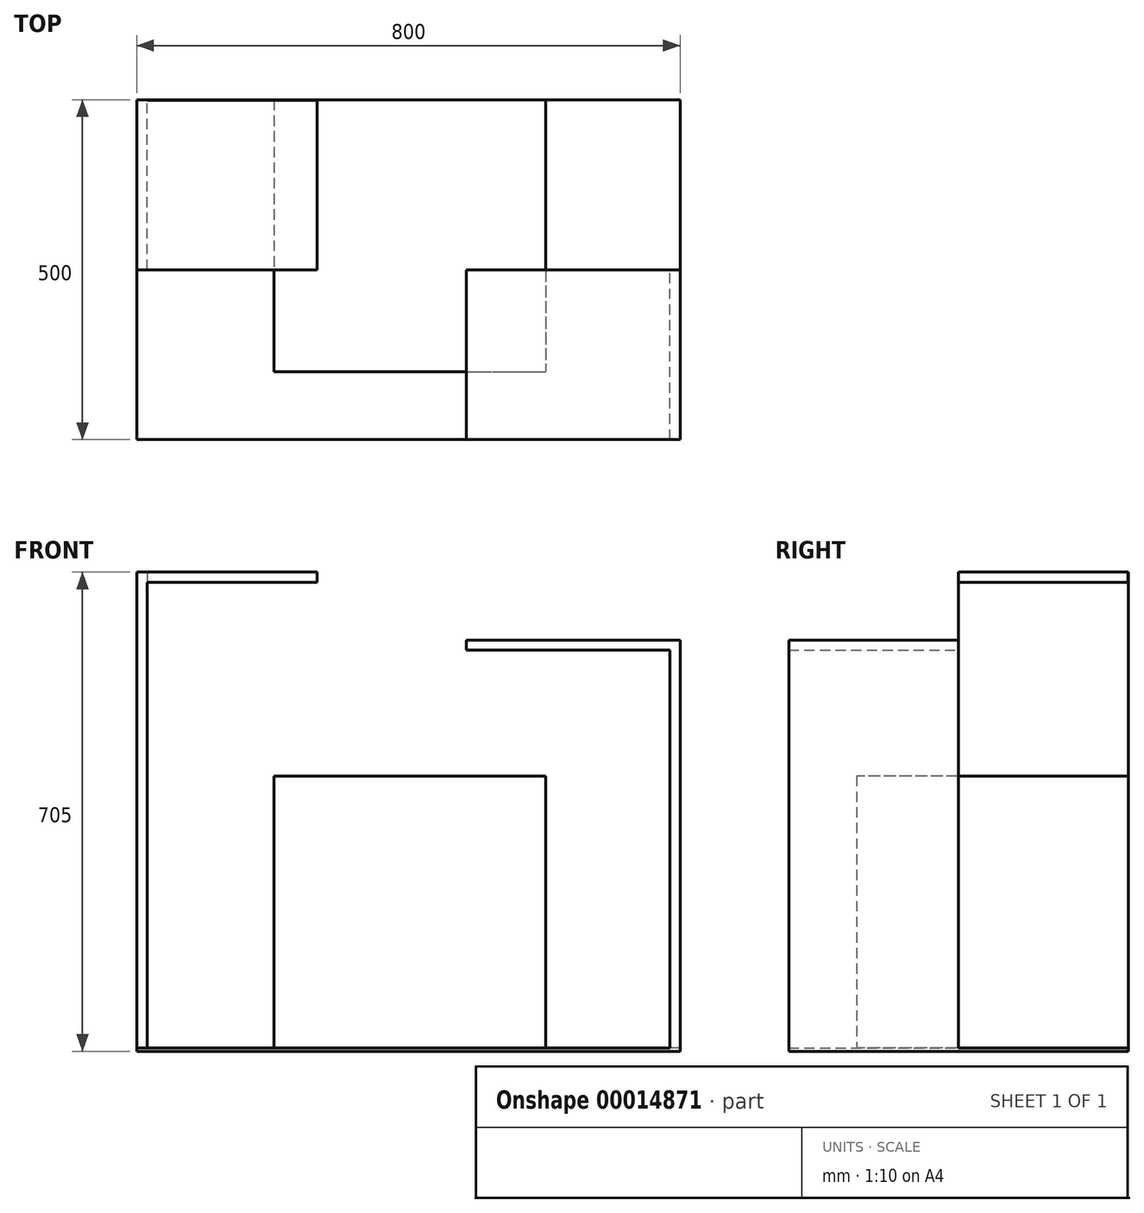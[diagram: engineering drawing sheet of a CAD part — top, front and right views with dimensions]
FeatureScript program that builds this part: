
annotation { "Feature Type Name" : "Feature", "Feature Type Description" : "" }
export const myFeature = defineFeature(function(context is Context, id is Id, definition is map)
    precondition{}
    {
        {
            var Q0;
            Q0=qCreatedBy(makeId("Top.planeOp"),FACE);
            var sketch = newSketch(context, id + "F0", { "sketchPlane" : qUnion([Q0])});
            skLineSegment(sketch, "E0.rect.bottom", {"start": v(-400, 250) * mm, "end": v(400, 250) * mm});
            skLineSegment(sketch, "E0.rect.top", {"start": v(-400, -250) * mm, "end": v(400, -250) * mm});
            skLineSegment(sketch, "E0.rect.left", {"start": v(-400, 250) * mm, "end": v(-400, -250) * mm});
            skLineSegment(sketch, "E0.rect.right", {"start": v(400, 250) * mm, "end": v(400, -250) * mm});
            skPoint(sketch, "E0.rect.middle", {"position": v(0, 0) * mm});
            skSolve(sketch);
        }
        {
            var Q0;
            Q0 = qSketchRegion(id + "F0", true);
            extrude(context, id + "F1", {"entities" : qUnion([Q0]), "depth" : 5 * mm});
        }
        {
            var Q0;
            Q0=makeQuery(id+"F1.opExtrude","CAP_FACE",FACE,{"disambiguationData":[OSD([sQuery(id+"F0.wireOp",EDGE,"E0.rect.bottom"),sQuery(id+"F0.wireOp",EDGE,"E0.rect.top"),sQuery(id+"F0.wireOp",EDGE,"E0.rect.left"),sQuery(id+"F0.wireOp",EDGE,"E0.rect.right")])],"isStart":false});
            cPlane(context, id + "F2", {"entities" : qUnion([Q0]), "cplaneType" : CPlaneType.OFFSET, "offset" : 0 * mm, "width" : 150 * mm, "height" : 150 * mm});
        }
        {
            var Q0;
            Q0=qCreatedBy(id+"F2.planeOp",FACE);
            var sketch = newSketch(context, id + "F3", { "sketchPlane" : qUnion([Q0])});
            skLineSegment(sketch, "E1.bottom", {"start": v(-198.2, 250) * mm, "end": v(201.8, 250) * mm});
            skLineSegment(sketch, "E1.top", {"start": v(-198.2, -150) * mm, "end": v(201.8, -150) * mm});
            skLineSegment(sketch, "E1.left", {"start": v(-198.2, 250) * mm, "end": v(-198.2, -150) * mm});
            skLineSegment(sketch, "E1.right", {"start": v(201.8, 250) * mm, "end": v(201.8, -150) * mm});
            skSolve(sketch);
        }
        {
            var Q0;
            Q0=makeQuery(id+"F3.imprint","IMPRINT",FACE,{"disambiguationData":[TD([[makeQuery(id+"F3.imprint","IMPRINT",EDGE,{"derivedFrom":sQuery(id+"F3.wireOp",EDGE,"E1.bottom")}),-1.0]])]});
            extrude(context, id + "F4", {"entities" : qUnion([Q0]), "operationType" : NewBodyOperationType.ADD, "depth" : 400 * mm});
        }
        {
            var Q0;
            Q0=makeQuery(id+"F1.opExtrude","CAP_FACE",FACE,{"disambiguationData":[OSD([sQuery(id+"F0.wireOp",EDGE,"E0.rect.bottom"),sQuery(id+"F0.wireOp",EDGE,"E0.rect.top"),sQuery(id+"F0.wireOp",EDGE,"E0.rect.left"),sQuery(id+"F0.wireOp",EDGE,"E0.rect.right")])],"isStart":false});
            cPlane(context, id + "F5", {"entities" : qUnion([Q0]), "cplaneType" : CPlaneType.OFFSET, "offset" : 0 * mm, "width" : 150 * mm, "height" : 150 * mm});
        }
        {
            var Q0;
            Q0=qCreatedBy(id+"F5.planeOp",FACE);
            var sketch = newSketch(context, id + "F6", { "sketchPlane" : qUnion([Q0])});
            skLineSegment(sketch, "E2.bottom", {"start": v(400, -250) * mm, "end": v(385, -250) * mm});
            skLineSegment(sketch, "E2.top", {"start": v(400, 0) * mm, "end": v(385, 0) * mm});
            skLineSegment(sketch, "E2.left", {"start": v(400, -250) * mm, "end": v(400, 0) * mm});
            skLineSegment(sketch, "E2.right", {"start": v(385, -250) * mm, "end": v(385, 0) * mm});
            skSolve(sketch);
        }
        {
            var Q0;
            Q0=makeQuery(id+"F6.imprint","IMPRINT",FACE,{"disambiguationData":[TD([[makeQuery(id+"F6.imprint","IMPRINT",EDGE,{"derivedFrom":sQuery(id+"F6.wireOp",EDGE,"E2.bottom")}),-1.0]])]});
            extrude(context, id + "F7", {"entities" : qUnion([Q0]), "operationType" : NewBodyOperationType.ADD, "depth" : 600 * mm});
        }
        {
            var Q0;
            Q0=makeQuery(id+"F1.opExtrude","CAP_FACE",FACE,{"disambiguationData":[OSD([sQuery(id+"F0.wireOp",EDGE,"E0.rect.bottom"),sQuery(id+"F0.wireOp",EDGE,"E0.rect.top"),sQuery(id+"F0.wireOp",EDGE,"E0.rect.left"),sQuery(id+"F0.wireOp",EDGE,"E0.rect.right")])],"isStart":false});
            cPlane(context, id + "F8", {"entities" : qUnion([Q0]), "cplaneType" : CPlaneType.OFFSET, "offset" : 0 * mm, "width" : 150 * mm, "height" : 150 * mm});
        }
        {
            var Q0;
            Q0=qCreatedBy(id+"F8.planeOp",FACE);
            var sketch = newSketch(context, id + "F9", { "sketchPlane" : qUnion([Q0])});
            skLineSegment(sketch, "E3.bottom", {"start": v(-399.75, 249.97) * mm, "end": v(-384.75, 249.97) * mm});
            skLineSegment(sketch, "E3.top", {"start": v(-399.75, 0) * mm, "end": v(-384.75, 0) * mm});
            skLineSegment(sketch, "E3.left", {"start": v(-399.75, 249.97) * mm, "end": v(-399.75, 0) * mm});
            skLineSegment(sketch, "E3.right", {"start": v(-384.75, 249.97) * mm, "end": v(-384.75, 0) * mm});
            skSolve(sketch);
        }
        {
            var Q0;
            Q0=makeQuery(id+"F9.imprint","IMPRINT",FACE,{"disambiguationData":[TD([[makeQuery(id+"F9.imprint","IMPRINT",EDGE,{"derivedFrom":sQuery(id+"F9.wireOp",EDGE,"E3.bottom")}),-1.0]])]});
            extrude(context, id + "F10", {"entities" : qUnion([Q0]), "operationType" : NewBodyOperationType.ADD, "depth" : 700 * mm});
        }
        {
            var Q0;
            Q0=makeQuery(id+"F7.opExtrude","SWEPT_FACE",FACE,{"disambiguationData":[OSD([sQuery(id+"F6.wireOp",EDGE,"E2.right")])]});
            cPlane(context, id + "F11", {"entities" : qUnion([Q0]), "cplaneType" : CPlaneType.OFFSET, "offset" : 0 * mm, "width" : 150 * mm, "height" : 150 * mm});
        }
        {
            var Q0;
            Q0=qCreatedBy(id+"F11.planeOp",FACE);
            var sketch = newSketch(context, id + "F12", { "sketchPlane" : qUnion([Q0])});
            skLineSegment(sketch, "E4.bottom", {"start": v(250, 605) * mm, "end": v(0, 605) * mm});
            skLineSegment(sketch, "E4.top", {"start": v(250, 590) * mm, "end": v(0, 590) * mm});
            skLineSegment(sketch, "E4.left", {"start": v(250, 605) * mm, "end": v(250, 590) * mm});
            skLineSegment(sketch, "E4.right", {"start": v(0, 605) * mm, "end": v(0, 590) * mm});
            skSolve(sketch);
        }
        {
            var Q0;
            Q0=makeQuery(id+"F12.imprint","IMPRINT",FACE,{"disambiguationData":[TD([[makeQuery(id+"F12.imprint","IMPRINT",EDGE,{"derivedFrom":sQuery(id+"F12.wireOp",EDGE,"E4.bottom")}),1.0]])]});
            extrude(context, id + "F13", {"entities" : qUnion([Q0]), "operationType" : NewBodyOperationType.ADD, "depth" : 300 * mm});
        }
        {
            var Q0;
            Q0=makeQuery(id+"F10.opExtrude","SWEPT_FACE",FACE,{"disambiguationData":[OSD([sQuery(id+"F9.wireOp",EDGE,"E3.right")])]});
            cPlane(context, id + "F14", {"entities" : qUnion([Q0]), "cplaneType" : CPlaneType.OFFSET, "offset" : 0 * mm, "width" : 150 * mm, "height" : 150 * mm});
        }
        {
            var Q0;
            Q0=qCreatedBy(id+"F14.planeOp",FACE);
            var sketch = newSketch(context, id + "F15", { "sketchPlane" : qUnion([Q0])});
            skLineSegment(sketch, "E5.bottom", {"start": v(0, 705) * mm, "end": v(249.5, 705) * mm});
            skLineSegment(sketch, "E5.top", {"start": v(0, 690) * mm, "end": v(249.5, 690) * mm});
            skLineSegment(sketch, "E5.left", {"start": v(0, 705) * mm, "end": v(0, 690) * mm});
            skLineSegment(sketch, "E5.right", {"start": v(249.5, 705) * mm, "end": v(249.5, 690) * mm});
            skSolve(sketch);
        }
        {
            var Q0;
            Q0=makeQuery(id+"F15.imprint","IMPRINT",FACE,{"disambiguationData":[TD([[makeQuery(id+"F15.imprint","IMPRINT",EDGE,{"derivedFrom":sQuery(id+"F15.wireOp",EDGE,"E5.bottom")}),-1.0]])]});
            extrude(context, id + "F16", {"entities" : qUnion([Q0]), "operationType" : NewBodyOperationType.ADD, "depth" : 250 * mm});
        }
    });
